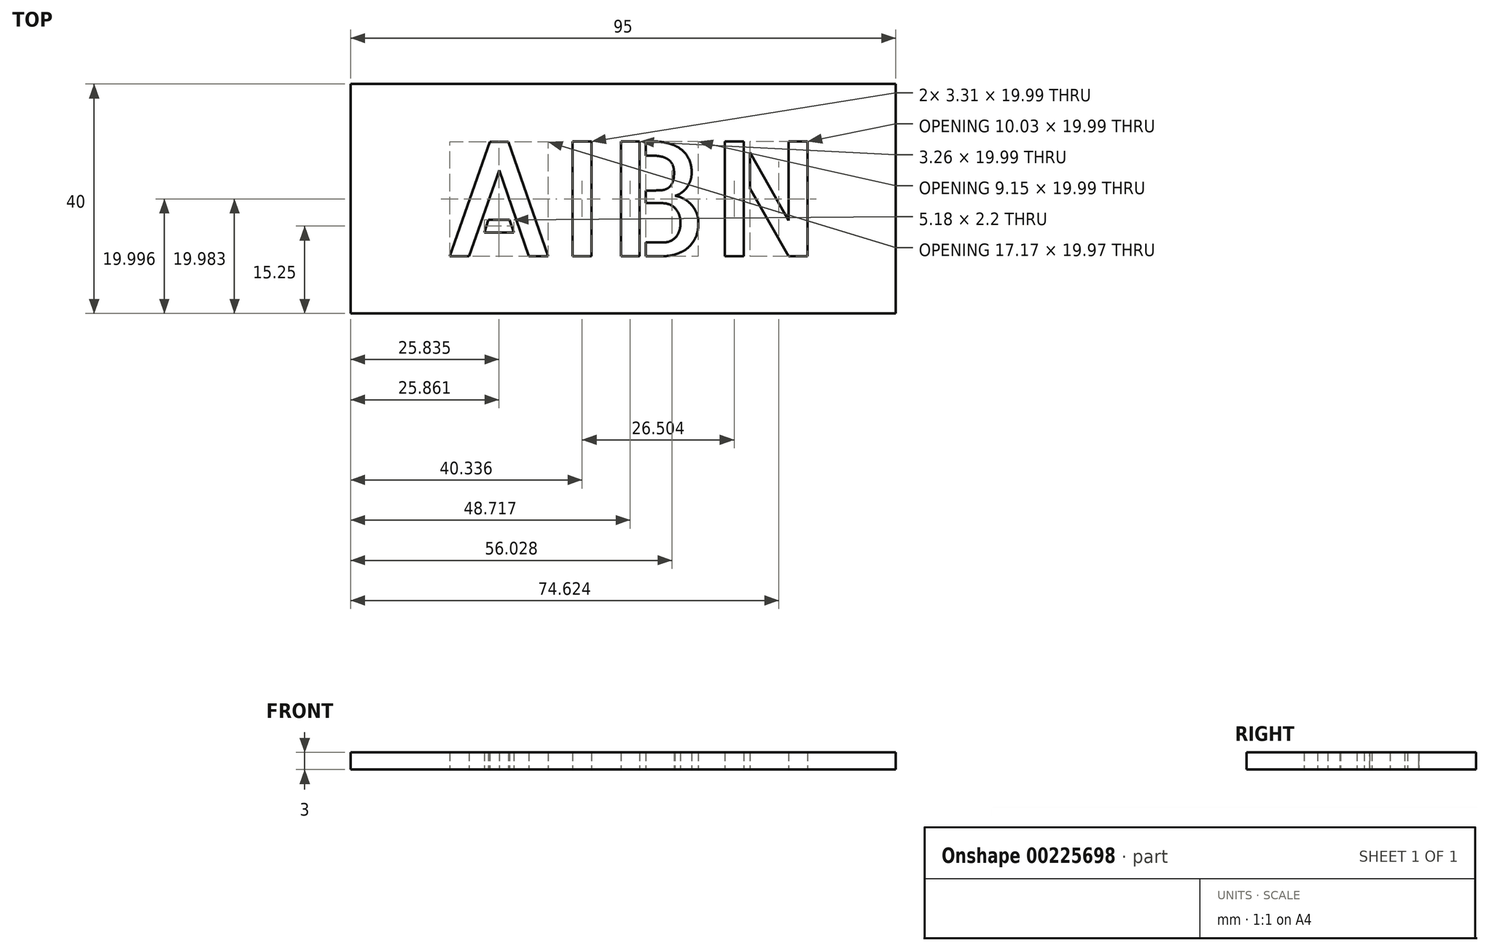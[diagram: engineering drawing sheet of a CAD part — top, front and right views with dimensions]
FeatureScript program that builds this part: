
annotation { "Feature Type Name" : "Feature", "Feature Type Description" : "" }
export const myFeature = defineFeature(function(context is Context, id is Id, definition is map)
    precondition{}
    {
        {
            var Q0;
            Q0=qCreatedBy(makeId("Top.planeOp"),FACE);
            var sketch = newSketch(context, id + "F0", { "sketchPlane" : qUnion([Q0])});
            skLineSegment(sketch, "E0", {"start": v(0, 0) * mm, "end": v(0, 20) * mm});
            skLineSegment(sketch, "E1.bottom", {"start": v(79.46, 30) * mm, "end": v(-15.54, 30) * mm});
            skLineSegment(sketch, "E1.top", {"start": v(79.46, -10) * mm, "end": v(-15.54, -10) * mm});
            skLineSegment(sketch, "E1.left", {"start": v(79.46, 30) * mm, "end": v(79.46, -10) * mm});
            skLineSegment(sketch, "E1.right", {"start": v(-15.54, 30) * mm, "end": v(-15.54, -10) * mm});
            skPoint(sketch, "E1.middle", {"position": v(31.96, 10) * mm});
            skText(sketch, "E2", { "text": "AIBN", "fontName": "AllertaStencil-Regular.ttf"});
            const initialGuessF0  = {"E2": [0, 0, 1, 0, 0.02]};
            skSetInitialGuess(sketch, initialGuessF0);
            skSolve(sketch);
        }
        {
            var Q0;
            Q0=makeQuery(id+"F0.imprint","IMPRINT",FACE,{"disambiguationData":[TD([[makeQuery(id+"F0.imprint","IMPRINT",EDGE,{"derivedFrom":sQuery(id+"F0.wireOp",EDGE,"E1.bottom")}),1.0]])]});
            extrude(context, id + "F1", {"entities" : qUnion([Q0]), "depth" : 3 * mm});
        }
    });
